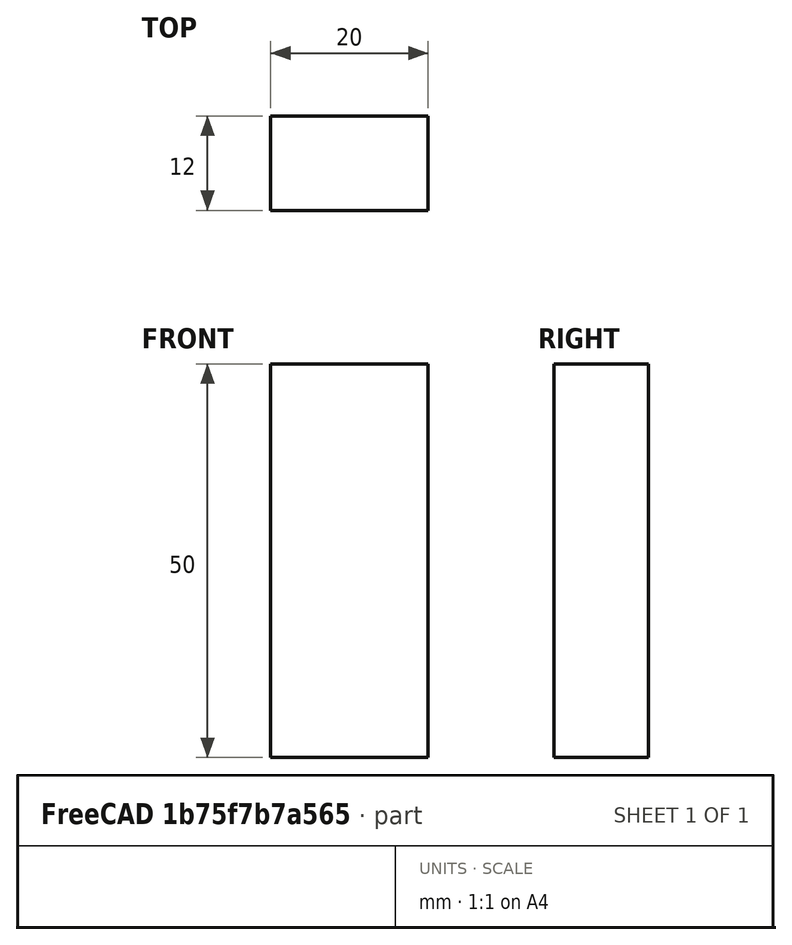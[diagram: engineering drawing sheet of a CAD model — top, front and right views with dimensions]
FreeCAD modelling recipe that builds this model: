
FCSTD DOCUMENT  (FreeCAD 0.15R4671 (Git))
Label: Flat Bar 20x12 EN10058 S235JR
License: All rights reserved
LicenseURL: http://en.wikipedia.org/wiki/All_rights_reserved
objects: Sketcher::SketchObject×1, Part::Extrusion×1
note: 2 computed .brp shape members not serialized (recipe doc carries the construction recipe); baked Part::Feature solids carry a one-line shape summary decoded from their .brp

FEATURE [Sketcher::SketchObject] Sketch
  sketch-geometry (4):
    g0: LineSegment StartX=-10 StartY=-6 StartZ=0 EndX=10 EndY=-6 EndZ=0
    g1: LineSegment StartX=10 StartY=-6 StartZ=0 EndX=10 EndY=6 EndZ=0
    g2: LineSegment StartX=10 StartY=6 StartZ=0 EndX=-10 EndY=6 EndZ=0
    g3: LineSegment StartX=-10 StartY=6 StartZ=0 EndX=-10 EndY=-6 EndZ=0
  constraints (12):
    c: Coincident(g0,g1)
    c: Coincident(g1,g2)
    c: Coincident(g2,g3)
    c: Coincident(g3,g0)
    c: Horizontal(g0)
    c: Horizontal(g2)
    c: Vertical(g1)
    c: Vertical(g3)
    c: Symmetric(g1,g2,g-2)
    c: Symmetric(g0,g1,g-1)
    c: DistanceY(g1) = 12
    c: DistanceX(g0) = 20
FEATURE [Part::Extrusion] Extrude  label="Flat Bar 20x12 EN10058 S235JR"
  Base = -> Sketch
  Dir = (0,0,50)
  Solid = true
